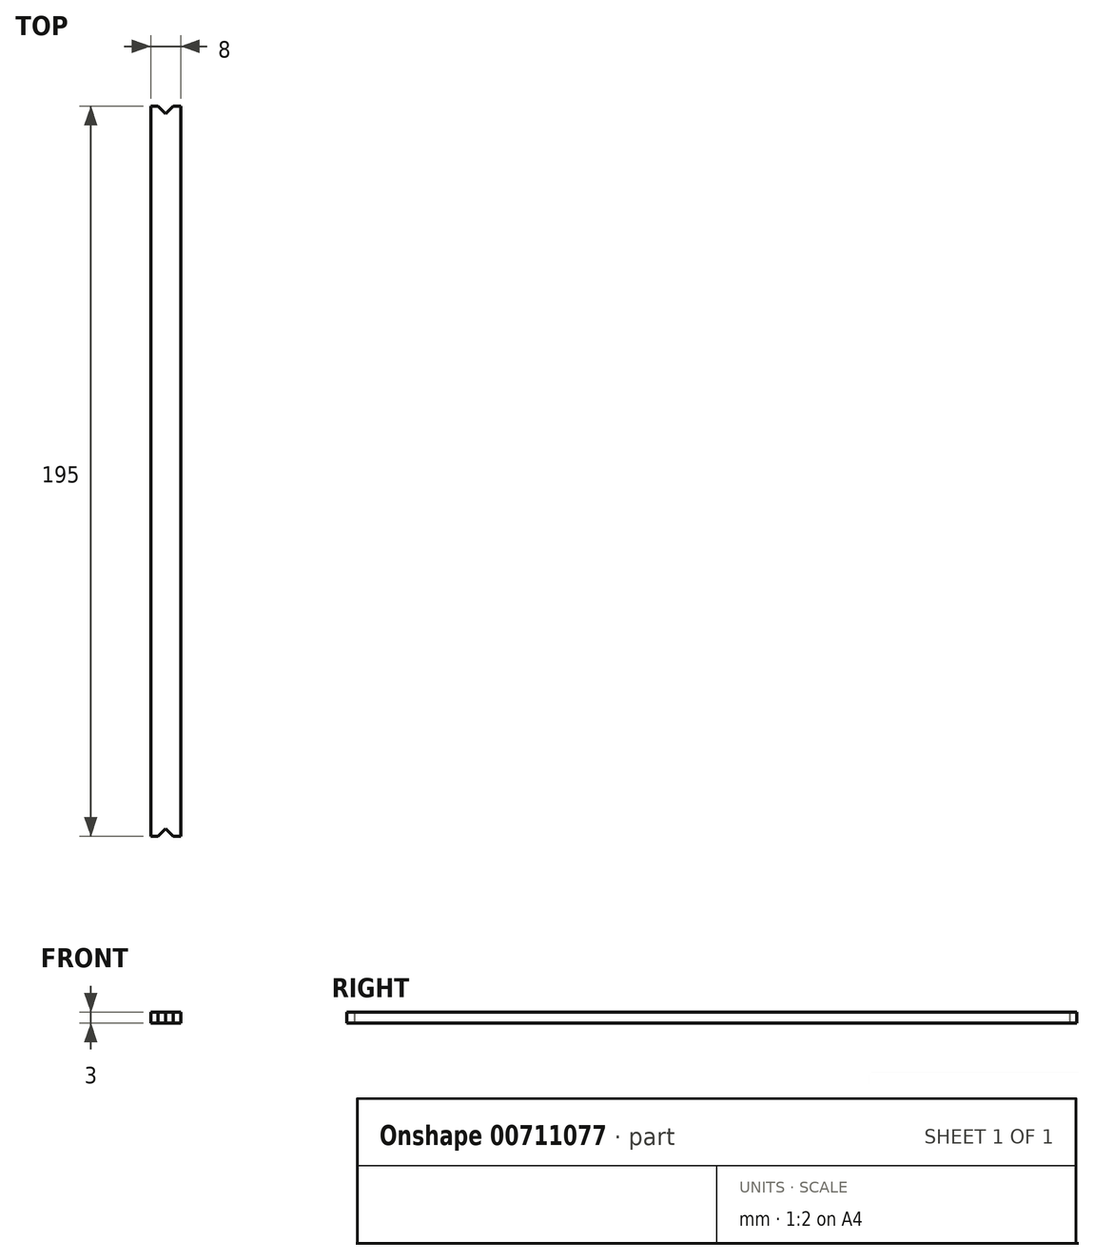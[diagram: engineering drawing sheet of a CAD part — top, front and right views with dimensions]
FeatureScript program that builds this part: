
annotation { "Feature Type Name" : "Feature", "Feature Type Description" : "" }
export const myFeature = defineFeature(function(context is Context, id is Id, definition is map)
    precondition{}
    {
        {
            var Q0;
            Q0=qCreatedBy(makeId("Top.planeOp"),FACE);
            var sketch = newSketch(context, id + "F0", { "sketchPlane" : qUnion([Q0])});
            skLineSegment(sketch, "E0.bottom", {"start": v(0, 0) * mm, "end": v(8, 0) * mm});
            skLineSegment(sketch, "E0.top", {"start": v(0, 195) * mm, "end": v(8, 195) * mm});
            skLineSegment(sketch, "E0.left", {"start": v(0, 0) * mm, "end": v(0, 195) * mm});
            skLineSegment(sketch, "E0.right", {"start": v(8, 0) * mm, "end": v(8, 195) * mm});
            skCircle(sketch, "E1.cCircle", {"center": v(4, 0) * mm, "radius": 1.41 * mm, "construction": true});
            skLineSegment(sketch, "E1.0", {"start": v(6, 0) * mm, "end": v(4, -2) * mm});
            skLineSegment(sketch, "E1.1", {"start": v(4, -2) * mm, "end": v(2, 0) * mm});
            skLineSegment(sketch, "E1.2", {"start": v(2, 0) * mm, "end": v(4, 2) * mm});
            skLineSegment(sketch, "E1.3", {"start": v(4, 2) * mm, "end": v(6, 0) * mm});
            skPoint(sketch, "E1.0.midPoint", {"position": v(5, -1) * mm});
            skCircle(sketch, "E2.cCircle", {"center": v(4, 195) * mm, "radius": 1.41 * mm, "construction": true});
            skLineSegment(sketch, "E2.0", {"start": v(6, 195) * mm, "end": v(4, 193) * mm});
            skLineSegment(sketch, "E2.1", {"start": v(4, 193) * mm, "end": v(2, 195) * mm});
            skLineSegment(sketch, "E2.2", {"start": v(2, 195) * mm, "end": v(4, 197) * mm});
            skLineSegment(sketch, "E2.3", {"start": v(4, 197) * mm, "end": v(6, 195) * mm});
            skPoint(sketch, "E2.0.midPoint", {"position": v(5, 194) * mm});
            skSolve(sketch);
        }
        {
            var Q0;
            {var subQ0=sQuery(id+"F0.wireOp",EDGE,"E0.left");Q0=makeQuery(id+"F0.imprint","IMPRINT",FACE,{"disambiguationData":[TD([[makeQuery(id+"F0.imprint","IMPRINT",EDGE,{"derivedFrom":subQ0}),-1.0]])]});}
            extrude(context, id + "F1", {"entities" : qUnion([Q0]), "depth" : 3 * mm, "offsetDistance" : 25 * mm});
        }
    });
